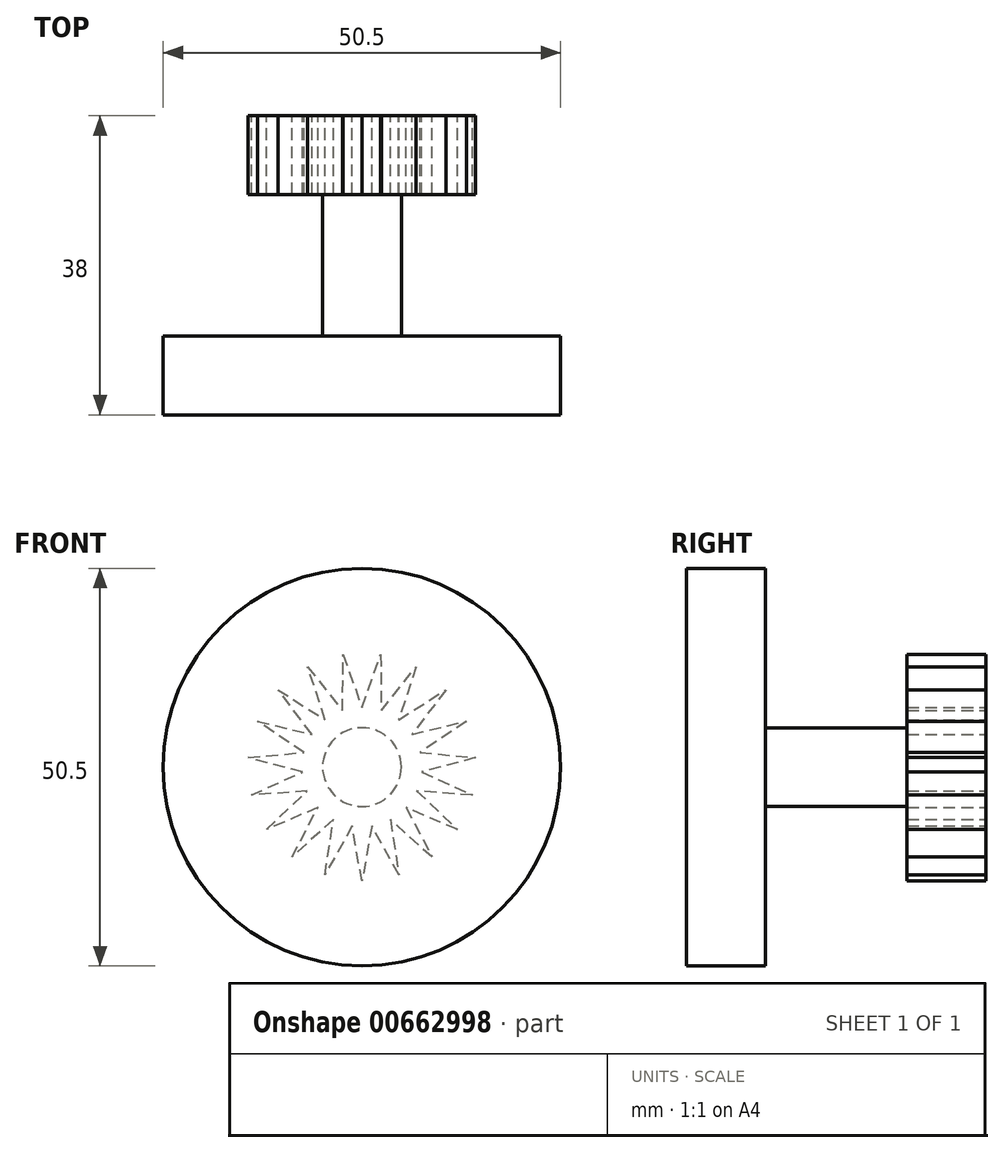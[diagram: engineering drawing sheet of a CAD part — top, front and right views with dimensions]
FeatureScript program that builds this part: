
annotation { "Feature Type Name" : "Feature", "Feature Type Description" : "" }
export const myFeature = defineFeature(function(context is Context, id is Id, definition is map)
    precondition{}
    {
        {
            var Q0;
            Q0=qCreatedBy(makeId("Front.planeOp"),FACE);
            var sketch = newSketch(context, id + "F0", { "sketchPlane" : qUnion([Q0])});
            skCircle(sketch, "E0", {"center": v(0, 0) * mm, "radius": 7.6 * mm, "construction": true});
            skLineSegment(sketch, "E1", {"start": v(0, 7.6) * mm, "end": v(2.39, 14.3) * mm});
            skLineSegment(sketch, "E2", {"start": v(2.39, 14.3) * mm, "end": v(2.47, 7.18) * mm});
            skLineSegment(sketch, "E3", {"start": v(0, 7.6) * mm, "end": v(1.25, 7.5) * mm, "construction": true});
            skLineSegment(sketch, "E4", {"start": v(1.25, 7.5) * mm, "end": v(2.47, 7.18) * mm, "construction": true});
            skLineSegment(sketch, "E5", {"start": v(0, 7.6) * mm, "end": v(2.47, 7.18) * mm, "construction": true});
            skLineSegment(sketch, "E6", {"start": v(2.39, 14.3) * mm, "end": v(1.23, 7.39) * mm, "construction": true});
            skLineSegment(sketch, "E7.1.0", {"start": v(-2.47, 7.18) * mm, "end": v(-2.39, 14.3) * mm});
            skLineSegment(sketch, "E7.1.1", {"start": v(-2.39, 14.3) * mm, "end": v(0, 7.6) * mm});
            skLineSegment(sketch, "E7.2.0", {"start": v(-4.66, 6) * mm, "end": v(-6.9, 12.74) * mm});
            skLineSegment(sketch, "E7.2.1", {"start": v(-6.9, 12.74) * mm, "end": v(-2.47, 7.18) * mm});
            skLineSegment(sketch, "E7.3.0", {"start": v(-6.36, 4.15) * mm, "end": v(-10.66, 9.81) * mm});
            skLineSegment(sketch, "E7.3.1", {"start": v(-10.66, 9.81) * mm, "end": v(-4.66, 6) * mm});
            skLineSegment(sketch, "E7.4.0", {"start": v(-7.36, 1.86) * mm, "end": v(-13.27, 5.82) * mm});
            skLineSegment(sketch, "E7.4.1", {"start": v(-13.27, 5.82) * mm, "end": v(-6.36, 4.15) * mm});
            skLineSegment(sketch, "E7.5.0", {"start": v(-7.57, -0.63) * mm, "end": v(-14.44, 1.2) * mm});
            skLineSegment(sketch, "E7.5.1", {"start": v(-14.44, 1.2) * mm, "end": v(-7.36, 1.86) * mm});
            skLineSegment(sketch, "E7.6.0", {"start": v(-6.95, -3.05) * mm, "end": v(-14.05, -3.56) * mm});
            skLineSegment(sketch, "E7.6.1", {"start": v(-14.05, -3.56) * mm, "end": v(-7.57, -0.63) * mm});
            skLineSegment(sketch, "E7.7.0", {"start": v(-5.59, -5.14) * mm, "end": v(-12.13, -7.93) * mm});
            skLineSegment(sketch, "E7.7.1", {"start": v(-12.13, -7.93) * mm, "end": v(-6.95, -3.05) * mm});
            skLineSegment(sketch, "E7.8.0", {"start": v(-3.61, -6.68) * mm, "end": v(-8.9, -11.44) * mm});
            skLineSegment(sketch, "E7.8.1", {"start": v(-8.9, -11.44) * mm, "end": v(-5.59, -5.14) * mm});
            skLineSegment(sketch, "E7.9.0", {"start": v(-1.25, -7.5) * mm, "end": v(-4.7, -13.7) * mm});
            skLineSegment(sketch, "E7.9.1", {"start": v(-4.7, -13.7) * mm, "end": v(-3.61, -6.68) * mm});
            skLineSegment(sketch, "E8.0.10.0", {"start": v(1.25, -7.5) * mm, "end": v(0, -14.5) * mm});
            skLineSegment(sketch, "E8.3.10.0", {"start": v(0, -14.5) * mm, "end": v(-1.25, -7.5) * mm});
            skLineSegment(sketch, "E8.0.11.0", {"start": v(3.61, -6.68) * mm, "end": v(4.7, -13.7) * mm});
            skLineSegment(sketch, "E8.3.11.0", {"start": v(4.7, -13.7) * mm, "end": v(1.25, -7.5) * mm});
            skLineSegment(sketch, "E8.0.12.0", {"start": v(5.59, -5.14) * mm, "end": v(8.9, -11.44) * mm});
            skLineSegment(sketch, "E8.3.12.0", {"start": v(8.9, -11.44) * mm, "end": v(3.61, -6.68) * mm});
            skLineSegment(sketch, "E8.0.13.0", {"start": v(6.95, -3.05) * mm, "end": v(12.13, -7.93) * mm});
            skLineSegment(sketch, "E8.3.13.0", {"start": v(12.13, -7.93) * mm, "end": v(5.59, -5.14) * mm});
            skLineSegment(sketch, "E8.0.14.0", {"start": v(7.57, -0.63) * mm, "end": v(14.05, -3.56) * mm});
            skLineSegment(sketch, "E8.3.14.0", {"start": v(14.05, -3.56) * mm, "end": v(6.95, -3.05) * mm});
            skLineSegment(sketch, "E9.0.15.0", {"start": v(7.36, 1.86) * mm, "end": v(14.44, 1.2) * mm});
            skLineSegment(sketch, "E9.3.15.0", {"start": v(14.44, 1.2) * mm, "end": v(7.57, -0.63) * mm});
            skLineSegment(sketch, "E10.0.16.0", {"start": v(6.36, 4.15) * mm, "end": v(13.27, 5.82) * mm});
            skLineSegment(sketch, "E10.3.16.0", {"start": v(13.27, 5.82) * mm, "end": v(7.36, 1.86) * mm});
            skLineSegment(sketch, "E10.0.17.0", {"start": v(4.66, 6) * mm, "end": v(10.66, 9.81) * mm});
            skLineSegment(sketch, "E10.3.17.0", {"start": v(10.66, 9.81) * mm, "end": v(6.36, 4.15) * mm});
            skLineSegment(sketch, "E11.0.18.0", {"start": v(2.47, 7.18) * mm, "end": v(6.9, 12.74) * mm});
            skLineSegment(sketch, "E11.3.18.0", {"start": v(6.9, 12.74) * mm, "end": v(4.66, 6) * mm});
            skSolve(sketch);
        }
        {
            var Q0;
            {var subQ15=sQuery(id+"F0.wireOp",EDGE,"E7.1.1");var subQ16=sQuery(id+"F0.wireOp",EDGE,"E1");var subQ17=makeQuery(id+"F0.imprint","INTERSECT",VERTEX,{"derivedFrom":[subQ16,subQ15]});Q0=makeQuery(id+"F0.imprint","IMPRINT",FACE,{"disambiguationData":[TD([[makeQuery(id+"F0.imprint","IMPRINT",EDGE,{"disambiguationData":[TD([[subQ17,-1.0]])],"derivedFrom":subQ16}),-1.0]])]});}
            extrude(context, id + "F1", {"entities" : qUnion([Q0]), "depth" : 10 * mm, "offsetDistance" : 25 * mm});
        }
        {
            var Q0;
            Q0=makeQuery(id+"F1.opExtrude","CAP_FACE",FACE,{"disambiguationData":[OSD([sQuery(id+"F0.wireOp",EDGE,"E1"),sQuery(id+"F0.wireOp",EDGE,"E2"),sQuery(id+"F0.wireOp",EDGE,"E7.1.0"),sQuery(id+"F0.wireOp",EDGE,"E7.1.1"),sQuery(id+"F0.wireOp",EDGE,"E7.2.0"),sQuery(id+"F0.wireOp",EDGE,"E7.2.1"),sQuery(id+"F0.wireOp",EDGE,"E7.3.0"),sQuery(id+"F0.wireOp",EDGE,"E7.3.1"),sQuery(id+"F0.wireOp",EDGE,"E7.4.0"),sQuery(id+"F0.wireOp",EDGE,"E7.4.1"),sQuery(id+"F0.wireOp",EDGE,"E7.5.0"),sQuery(id+"F0.wireOp",EDGE,"E7.5.1"),sQuery(id+"F0.wireOp",EDGE,"E7.6.0"),sQuery(id+"F0.wireOp",EDGE,"E7.6.1"),sQuery(id+"F0.wireOp",EDGE,"E7.7.0"),sQuery(id+"F0.wireOp",EDGE,"E7.7.1"),sQuery(id+"F0.wireOp",EDGE,"E7.8.0"),sQuery(id+"F0.wireOp",EDGE,"E7.8.1"),sQuery(id+"F0.wireOp",EDGE,"E7.9.0"),sQuery(id+"F0.wireOp",EDGE,"E7.9.1")])],"isStart":false});
            var sketch = newSketch(context, id + "F2", { "sketchPlane" : qUnion([Q0])});
            skCircle(sketch, "E12", {"center": v(0, 0) * mm, "radius": 5 * mm});
            skSolve(sketch);
        }
        {
            var Q0;
            Q0=makeQuery(id+"F2.imprint","IMPRINT",FACE,{"disambiguationData":[TD([[makeQuery(id+"F2.imprint","IMPRINT",EDGE,{"derivedFrom":sQuery(id+"F2.wireOp",EDGE,"E12")}),1.0]])]});
            extrude(context, id + "F3", {"entities" : qUnion([Q0]), "operationType" : NewBodyOperationType.ADD, "depth" : 18 * mm, "offsetDistance" : 25 * mm});
        }
        {
            var Q0;
            Q0=makeQuery(id+"F3.opExtrude","CAP_FACE",FACE,{"disambiguationData":[OSD([sQuery(id+"F2.wireOp",EDGE,"E12")])],"isStart":false});
            var sketch = newSketch(context, id + "F4", { "sketchPlane" : qUnion([Q0])});
            skCircle(sketch, "E13", {"center": v(0, 0) * mm, "radius": 25.25 * mm});
            skSolve(sketch);
        }
        {
            var Q0;
            Q0=makeQuery(id+"F4.imprint","IMPRINT",FACE,{"disambiguationData":[TD([[makeQuery(id+"F4.imprint","IMPRINT",EDGE,{"derivedFrom":makeQuery(id+"F3.opExtrude","CAP_EDGE",EDGE,{"disambiguationData":[OSD([sQuery(id+"F2.wireOp",EDGE,"E12")])],"isStart":false})}),1.0]])]});
            var Q1;
            Q1=makeQuery(id+"F4.imprint","IMPRINT",FACE,{"disambiguationData":[TD([[makeQuery(id+"F4.imprint","IMPRINT",EDGE,{"derivedFrom":sQuery(id+"F4.wireOp",EDGE,"E13")}),1.0]])]});
            extrude(context, id + "F5", {"entities" : qUnion([Q0, Q1]), "operationType" : NewBodyOperationType.ADD, "depth" : (38 - 10 - 18) * mm, "offsetDistance" : 25 * mm});
        }
    });
